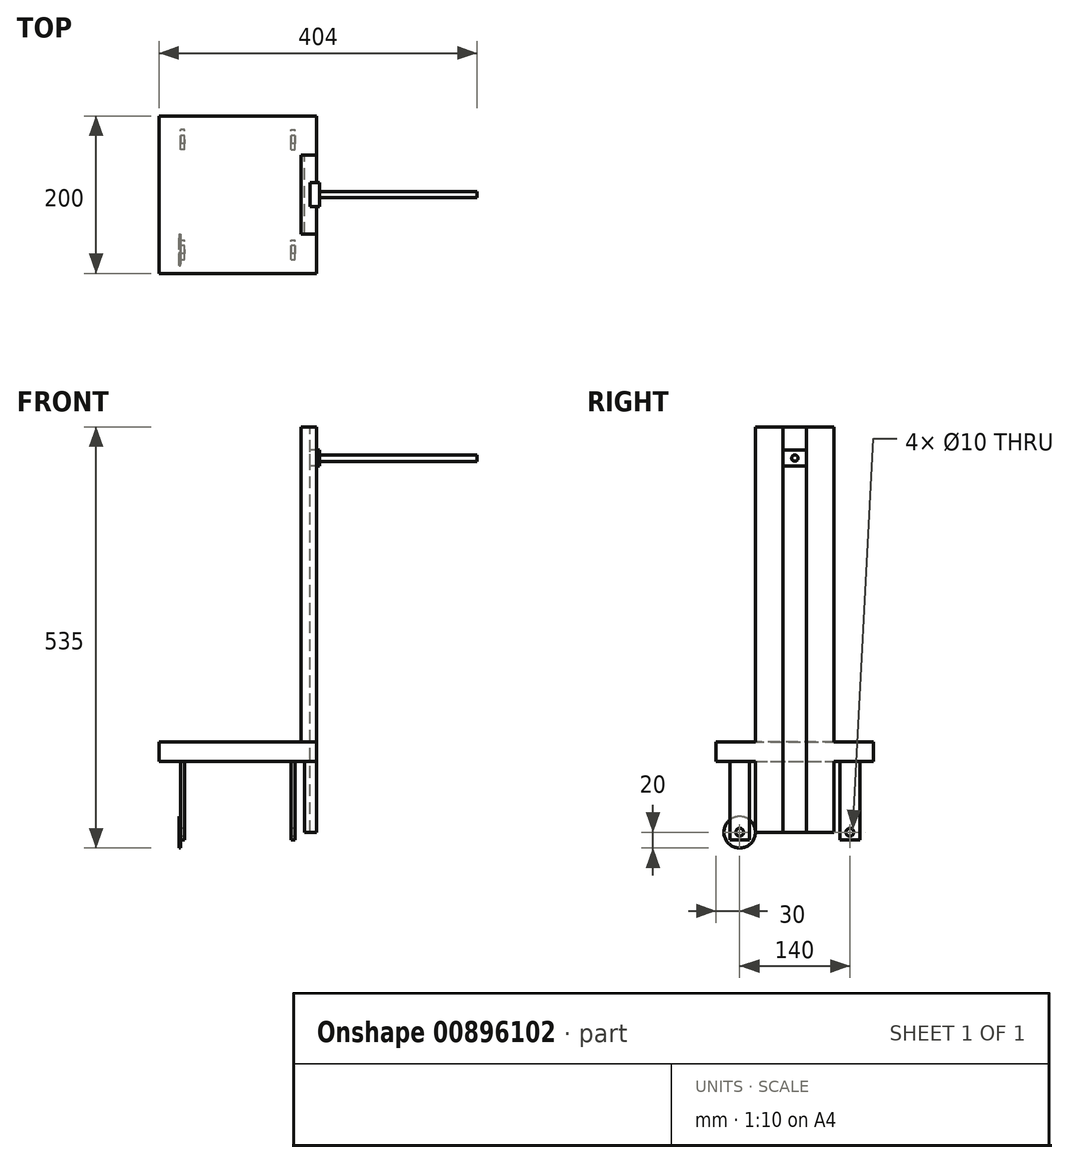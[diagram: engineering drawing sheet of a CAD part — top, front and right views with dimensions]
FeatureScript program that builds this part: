
annotation { "Feature Type Name" : "Feature", "Feature Type Description" : "" }
export const myFeature = defineFeature(function(context is Context, id is Id, definition is map)
    precondition{}
    {
        {
            var Q0;
            Q0=qCreatedBy(makeId("Top.planeOp"),FACE);
            var sketch = newSketch(context, id + "F0", { "sketchPlane" : qUnion([Q0])});
            skLineSegment(sketch, "E0.bottom", {"start": v(0, 0) * mm, "end": v(-200, 0) * mm});
            skLineSegment(sketch, "E0.top", {"start": v(0, 200) * mm, "end": v(-200, 200) * mm});
            skLineSegment(sketch, "E0.left", {"start": v(0, 0) * mm, "end": v(0, 200) * mm});
            skLineSegment(sketch, "E0.right", {"start": v(-200, 0) * mm, "end": v(-200, 200) * mm});
            skSolve(sketch);
        }
        {
            var Q0;
            Q0 = qSketchRegion(id + "F0", true);
            extrude(context, id + "F1", {"entities" : qUnion([Q0]), "depth" : 25 * mm, "offsetDistance" : 25 * mm});
        }
        {
            var Q0;
            Q0=makeQuery(id+"F1.opExtrude","CAP_FACE",FACE,{"disambiguationData":[OSD([sQuery(id+"F0.wireOp",EDGE,"E0.bottom"),sQuery(id+"F0.wireOp",EDGE,"E0.top"),sQuery(id+"F0.wireOp",EDGE,"E0.left"),sQuery(id+"F0.wireOp",EDGE,"E0.right")])],"isStart":true});
            var sketch = newSketch(context, id + "F2", { "sketchPlane" : qUnion([Q0])});
            skLineSegment(sketch, "E1", {"start": v(-170, 0) * mm, "end": v(-170, -30) * mm, "construction": true});
            skLineSegment(sketch, "E2", {"start": v(-170, -30) * mm, "end": v(-200, -30) * mm, "construction": true});
            skLineSegment(sketch, "E3.bottom", {"start": v(-172.5, -17.5) * mm, "end": v(-167.5, -17.5) * mm});
            skLineSegment(sketch, "E3.top", {"start": v(-172.5, -42.5) * mm, "end": v(-167.5, -42.5) * mm});
            skLineSegment(sketch, "E3.left", {"start": v(-172.5, -17.5) * mm, "end": v(-172.5, -42.5) * mm});
            skLineSegment(sketch, "E3.right", {"start": v(-167.5, -17.5) * mm, "end": v(-167.5, -42.5) * mm});
            skPoint(sketch, "E3.middle", {"position": v(-170, -30) * mm});
            skLineSegment(sketch, "E4", {"start": v(-30, 0) * mm, "end": v(-30, -30) * mm, "construction": true});
            skLineSegment(sketch, "E5", {"start": v(-30, -30) * mm, "end": v(0, -30) * mm, "construction": true});
            skLineSegment(sketch, "E6", {"start": v(0, -170) * mm, "end": v(-30, -170) * mm, "construction": true});
            skLineSegment(sketch, "E7", {"start": v(-30, -170) * mm, "end": v(-30, -200) * mm, "construction": true});
            skLineSegment(sketch, "E8", {"start": v(-200, -170) * mm, "end": v(-170, -170) * mm, "construction": true});
            skLineSegment(sketch, "E9", {"start": v(-170, -170) * mm, "end": v(-170, -200) * mm, "construction": true});
            skLineSegment(sketch, "E10.bottom", {"start": v(-167.5, -157.5) * mm, "end": v(-172.5, -157.5) * mm});
            skLineSegment(sketch, "E10.top", {"start": v(-167.5, -182.5) * mm, "end": v(-172.5, -182.5) * mm});
            skLineSegment(sketch, "E10.left", {"start": v(-167.5, -157.5) * mm, "end": v(-167.5, -182.5) * mm});
            skLineSegment(sketch, "E10.right", {"start": v(-172.5, -157.5) * mm, "end": v(-172.5, -182.5) * mm});
            skPoint(sketch, "E10.middle", {"position": v(-170, -170) * mm});
            skLineSegment(sketch, "E11.bottom", {"start": v(-32.5, -157.5) * mm, "end": v(-27.5, -157.5) * mm});
            skLineSegment(sketch, "E11.top", {"start": v(-32.5, -182.5) * mm, "end": v(-27.5, -182.5) * mm});
            skLineSegment(sketch, "E11.left", {"start": v(-32.5, -157.5) * mm, "end": v(-32.5, -182.5) * mm});
            skLineSegment(sketch, "E11.right", {"start": v(-27.5, -157.5) * mm, "end": v(-27.5, -182.5) * mm});
            skPoint(sketch, "E11.middle", {"position": v(-30, -170) * mm});
            skLineSegment(sketch, "E12.bottom", {"start": v(-32.5, -17.5) * mm, "end": v(-27.5, -17.5) * mm});
            skLineSegment(sketch, "E12.top", {"start": v(-32.5, -42.5) * mm, "end": v(-27.5, -42.5) * mm});
            skLineSegment(sketch, "E12.left", {"start": v(-32.5, -17.5) * mm, "end": v(-32.5, -42.5) * mm});
            skLineSegment(sketch, "E12.right", {"start": v(-27.5, -17.5) * mm, "end": v(-27.5, -42.5) * mm});
            skPoint(sketch, "E12.middle", {"position": v(-30, -30) * mm});
            skSolve(sketch);
        }
        {
            var Q0;
            Q0=makeQuery(id+"F2.imprint","IMPRINT",FACE,{"disambiguationData":[TD([[makeQuery(id+"F2.imprint","IMPRINT",EDGE,{"derivedFrom":sQuery(id+"F2.wireOp",EDGE,"E3.bottom")}),-1.0]])]});
            var Q1;
            Q1=makeQuery(id+"F2.imprint","IMPRINT",FACE,{"disambiguationData":[TD([[makeQuery(id+"F2.imprint","IMPRINT",EDGE,{"derivedFrom":sQuery(id+"F2.wireOp",EDGE,"E12.bottom")}),-1.0]])]});
            var Q2;
            Q2=makeQuery(id+"F2.imprint","IMPRINT",FACE,{"disambiguationData":[TD([[makeQuery(id+"F2.imprint","IMPRINT",EDGE,{"derivedFrom":sQuery(id+"F2.wireOp",EDGE,"E11.bottom")}),-1.0]])]});
            var Q3;
            Q3=makeQuery(id+"F2.imprint","IMPRINT",FACE,{"disambiguationData":[TD([[makeQuery(id+"F2.imprint","IMPRINT",EDGE,{"derivedFrom":sQuery(id+"F2.wireOp",EDGE,"E10.bottom")}),1.0]])]});
            extrude(context, id + "F3", {"entities" : qUnion([Q0, Q1, Q2, Q3]), "operationType" : NewBodyOperationType.ADD, "depth" : 100 * mm, "offsetDistance" : 25 * mm});
        }
        {
            var Q0;
            Q0=makeQuery(id+"F3.opExtrude","SWEPT_FACE",FACE,{"disambiguationData":[OSD([sQuery(id+"F2.wireOp",EDGE,"E3.left")])]});
            var sketch = newSketch(context, id + "F4", { "sketchPlane" : qUnion([Q0])});
            skLineSegment(sketch, "E13", {"start": v(-30, 0) * mm, "end": v(-30, -90) * mm, "construction": true});
            skCircle(sketch, "E14", {"center": v(-30, -90) * mm, "radius": 5 * mm});
            skSolve(sketch);
        }
        {
            var Q0;
            Q0=makeQuery(id+"F4.imprint","IMPRINT",FACE,{"disambiguationData":[TD([[makeQuery(id+"F4.imprint","IMPRINT",EDGE,{"derivedFrom":sQuery(id+"F4.wireOp",EDGE,"E14")}),1.0]])]});
            extrude(context, id + "F5", {"entities" : qUnion([Q0]), "operationType" : NewBodyOperationType.REMOVE, "endBound" : BoundingType.THROUGH_ALL, "oppositeDirection" : true, "depth" : 25 * mm, "offsetDistance" : 25 * mm});
        }
        {
            var Q0;
            Q0=makeQuery(id+"F3.opExtrude","SWEPT_FACE",FACE,{"disambiguationData":[OSD([sQuery(id+"F2.wireOp",EDGE,"E10.right")])]});
            var sketch = newSketch(context, id + "F6", { "sketchPlane" : qUnion([Q0])});
            skLineSegment(sketch, "E15", {"start": v(-170, 0) * mm, "end": v(-170, -90) * mm, "construction": true});
            skCircle(sketch, "E16", {"center": v(-170, -90) * mm, "radius": 5 * mm});
            skSolve(sketch);
        }
        {
            var Q0;
            Q0=makeQuery(id+"F6.imprint","IMPRINT",FACE,{"disambiguationData":[TD([[makeQuery(id+"F6.imprint","IMPRINT",EDGE,{"derivedFrom":sQuery(id+"F6.wireOp",EDGE,"E16")}),1.0]])]});
            var Q1;
            Q1=sQuery(id+"F6.wireOp",EDGE,"E16");
            extrude(context, id + "F7", {"entities" : qUnion([Q0]), "operationType" : NewBodyOperationType.REMOVE, "surfaceEntities" : qUnion([Q1]), "endBound" : BoundingType.THROUGH_ALL, "oppositeDirection" : true, "depth" : 25 * mm, "offsetDistance" : 25 * mm});
        }
        {
            var Q0;
            Q0=makeQuery(id+"F1.opExtrude","CAP_FACE",FACE,{"disambiguationData":[OSD([sQuery(id+"F0.wireOp",EDGE,"E0.bottom"),sQuery(id+"F0.wireOp",EDGE,"E0.top"),sQuery(id+"F0.wireOp",EDGE,"E0.left"),sQuery(id+"F0.wireOp",EDGE,"E0.right")])],"isStart":true});
            var sketch = newSketch(context, id + "F8", { "sketchPlane" : qUnion([Q0])});
            skLineSegment(sketch, "E17.left", {"start": v(-15.36, -50) * mm, "end": v(-15.36, -150) * mm});
            skPoint(sketch, "E17.middle", {"position": v(0, -100) * mm});
            skLineSegment(sketch, "E18", {"start": v(0, -50) * mm, "end": v(0, -150) * mm});
            skLineSegment(sketch, "E19", {"start": v(-15.36, -50) * mm, "end": v(0, -50) * mm});
            skLineSegment(sketch, "E20", {"start": v(-15.36, -150) * mm, "end": v(0, -150) * mm});
            skSolve(sketch);
        }
        {
            var Q0;
            Q0=makeQuery(id+"F8.imprint","IMPRINT",FACE,{"disambiguationData":[TD([[makeQuery(id+"F8.imprint","IMPRINT",EDGE,{"derivedFrom":sQuery(id+"F8.wireOp",EDGE,"E17.left")}),1.0]])]});
            extrude(context, id + "F9", {"entities" : qUnion([Q0]), "operationType" : NewBodyOperationType.ADD, "depth" : 90 * mm, "offsetDistance" : 25 * mm});
        }
        {
            var Q0;
            Q0=makeQuery(id+"F1.opExtrude","CAP_FACE",FACE,{"disambiguationData":[OSD([sQuery(id+"F0.wireOp",EDGE,"E0.bottom"),sQuery(id+"F0.wireOp",EDGE,"E0.top"),sQuery(id+"F0.wireOp",EDGE,"E0.left"),sQuery(id+"F0.wireOp",EDGE,"E0.right")])],"isStart":false});
            var sketch = newSketch(context, id + "F10", { "sketchPlane" : qUnion([Q0])});
            skLineSegment(sketch, "E21.bottom", {"start": v(-19.9, 150) * mm, "end": v(0, 150) * mm});
            skLineSegment(sketch, "E21.top", {"start": v(-19.9, 50) * mm, "end": v(0, 50) * mm});
            skLineSegment(sketch, "E21.left", {"start": v(-19.9, 150) * mm, "end": v(-19.9, 50) * mm});
            skPoint(sketch, "E21.middle", {"position": v(0, 100) * mm});
            skLineSegment(sketch, "E22", {"start": v(0, 150) * mm, "end": v(0, 50) * mm});
            skSolve(sketch);
        }
        {
            var Q0;
            Q0=makeQuery(id+"F10.imprint","IMPRINT",FACE,{"disambiguationData":[TD([[makeQuery(id+"F10.imprint","IMPRINT",EDGE,{"derivedFrom":sQuery(id+"F10.wireOp",EDGE,"E21.bottom")}),-1.0]])]});
            extrude(context, id + "F11", {"entities" : qUnion([Q0]), "operationType" : NewBodyOperationType.ADD, "depth" : 400 * mm, "offsetDistance" : 25 * mm});
        }
        {
            var Q0;
            Q0=makeQuery(id+"F11.boolean.opBoolean","MERGE",FACE,{"derivedFrom":[makeQuery(id+"F9.boolean.opBoolean","MERGE",FACE,{"derivedFrom":[makeQuery(id+"F1.opExtrude","SWEPT_FACE",FACE,{"disambiguationData":[OSD([sQuery(id+"F0.wireOp",EDGE,"E0.left")])]}),makeQuery(id+"F9.opExtrude","SWEPT_FACE",FACE,{"disambiguationData":[OSD([sQuery(id+"F8.wireOp",EDGE,"E18")])]})]}),makeQuery(id+"F11.opExtrude","SWEPT_FACE",FACE,{"disambiguationData":[OSD([sQuery(id+"F10.wireOp",EDGE,"E22")])]})]});
            var sketch = newSketch(context, id + "F12", { "sketchPlane" : qUnion([Q0])});
            skLineSegment(sketch, "E23.bottom", {"start": v(115, -90) * mm, "end": v(85, -90) * mm});
            skLineSegment(sketch, "E23.left", {"start": v(115, -90) * mm, "end": v(115, 425) * mm});
            skLineSegment(sketch, "E23.right", {"start": v(85, -90) * mm, "end": v(85, 425) * mm});
            skPoint(sketch, "E23.middle", {"position": v(100, 425) * mm});
            skLineSegment(sketch, "E24", {"start": v(85, 425) * mm, "end": v(115, 425) * mm});
            skSolve(sketch);
        }
        {
            var Q0;
            Q0=makeQuery(id+"F12.imprint","IMPRINT",FACE,{"disambiguationData":[TD([[makeQuery(id+"F12.imprint","IMPRINT",EDGE,{"derivedFrom":sQuery(id+"F12.wireOp",EDGE,"E23.bottom")}),1.0]])]});
            extrude(context, id + "F13", {"entities" : qUnion([Q0]), "operationType" : NewBodyOperationType.REMOVE, "oppositeDirection" : true, "depth" : 8 * mm, "offsetDistance" : 25 * mm});
        }
        {
            var Q0;
            Q0=makeQuery(id+"F13.boolean.opBoolean","COPY",FACE,{"derivedFrom":makeQuery(id+"F13.opExtrude","CAP_FACE",FACE,{"disambiguationData":[OSD([sQuery(id+"F12.wireOp",EDGE,"E23.bottom"),sQuery(id+"F12.wireOp",EDGE,"E23.left"),sQuery(id+"F12.wireOp",EDGE,"E23.right"),sQuery(id+"F12.wireOp",EDGE,"E24")])],"isStart":false})});
            var sketch = newSketch(context, id + "F14", { "sketchPlane" : qUnion([Q0])});
            skLineSegment(sketch, "E25.bottom", {"start": v(85, 395.25) * mm, "end": v(115, 395.25) * mm});
            skLineSegment(sketch, "E25.top", {"start": v(85, 375.23) * mm, "end": v(115, 375.23) * mm});
            skLineSegment(sketch, "E25.left", {"start": v(85, 395.25) * mm, "end": v(85, 375.23) * mm});
            skLineSegment(sketch, "E25.right", {"start": v(115, 395.25) * mm, "end": v(115, 375.23) * mm});
            skSolve(sketch);
        }
        {
            var Q0;
            Q0=makeQuery(id+"F14.imprint","IMPRINT",FACE,{"disambiguationData":[TD([[makeQuery(id+"F14.imprint","IMPRINT",EDGE,{"derivedFrom":sQuery(id+"F14.wireOp",EDGE,"E25.bottom")}),-1.0]])]});
            extrude(context, id + "F15", {"entities" : qUnion([Q0]), "depth" : 12 * mm, "offsetDistance" : 25 * mm});
        }
        {
            var Q0;
            Q0=makeQuery(id+"F15.opExtrude","CAP_FACE",FACE,{"disambiguationData":[OSD([sQuery(id+"F14.wireOp",EDGE,"E25.bottom"),sQuery(id+"F14.wireOp",EDGE,"E25.top"),sQuery(id+"F14.wireOp",EDGE,"E25.left"),sQuery(id+"F14.wireOp",EDGE,"E25.right")])],"isStart":false});
            var sketch = newSketch(context, id + "F16", { "sketchPlane" : qUnion([Q0])});
            skCircle(sketch, "E26", {"center": v(100, 385.24) * mm, "radius": 4 * mm});
            skPoint(sketch, "E26.centerSnap0", {"position": v(85, 385.24) * mm});
            skPoint(sketch, "E26.centerSnap1", {"position": v(100, 395.25) * mm});
            skSolve(sketch);
        }
        {
            var Q0;
            Q0=makeQuery(id+"F16.imprint","IMPRINT",FACE,{"disambiguationData":[TD([[makeQuery(id+"F16.imprint","IMPRINT",EDGE,{"derivedFrom":sQuery(id+"F16.wireOp",EDGE,"E26")}),1.0]])]});
            extrude(context, id + "F17", {"entities" : qUnion([Q0]), "operationType" : NewBodyOperationType.ADD, "depth" : 200 * mm, "offsetDistance" : 25 * mm});
        }
        {
            var Q0;
            Q0=makeQuery(id+"F3.opExtrude","SWEPT_FACE",FACE,{"disambiguationData":[OSD([sQuery(id+"F2.wireOp",EDGE,"E3.left")])]});
            var sketch = newSketch(context, id + "F18", { "sketchPlane" : qUnion([Q0])});
            skCircle(sketch, "E27", {"center": v(-30, -90) * mm, "radius": 20 * mm});
            skSolve(sketch);
        }
        {
            var Q0;
            Q0 = qSketchRegion(id + "F18", true);
            extrude(context, id + "F19", {"entities" : qUnion([Q0]), "depth" : 2 * mm, "offsetDistance" : 25 * mm});
        }
    });
